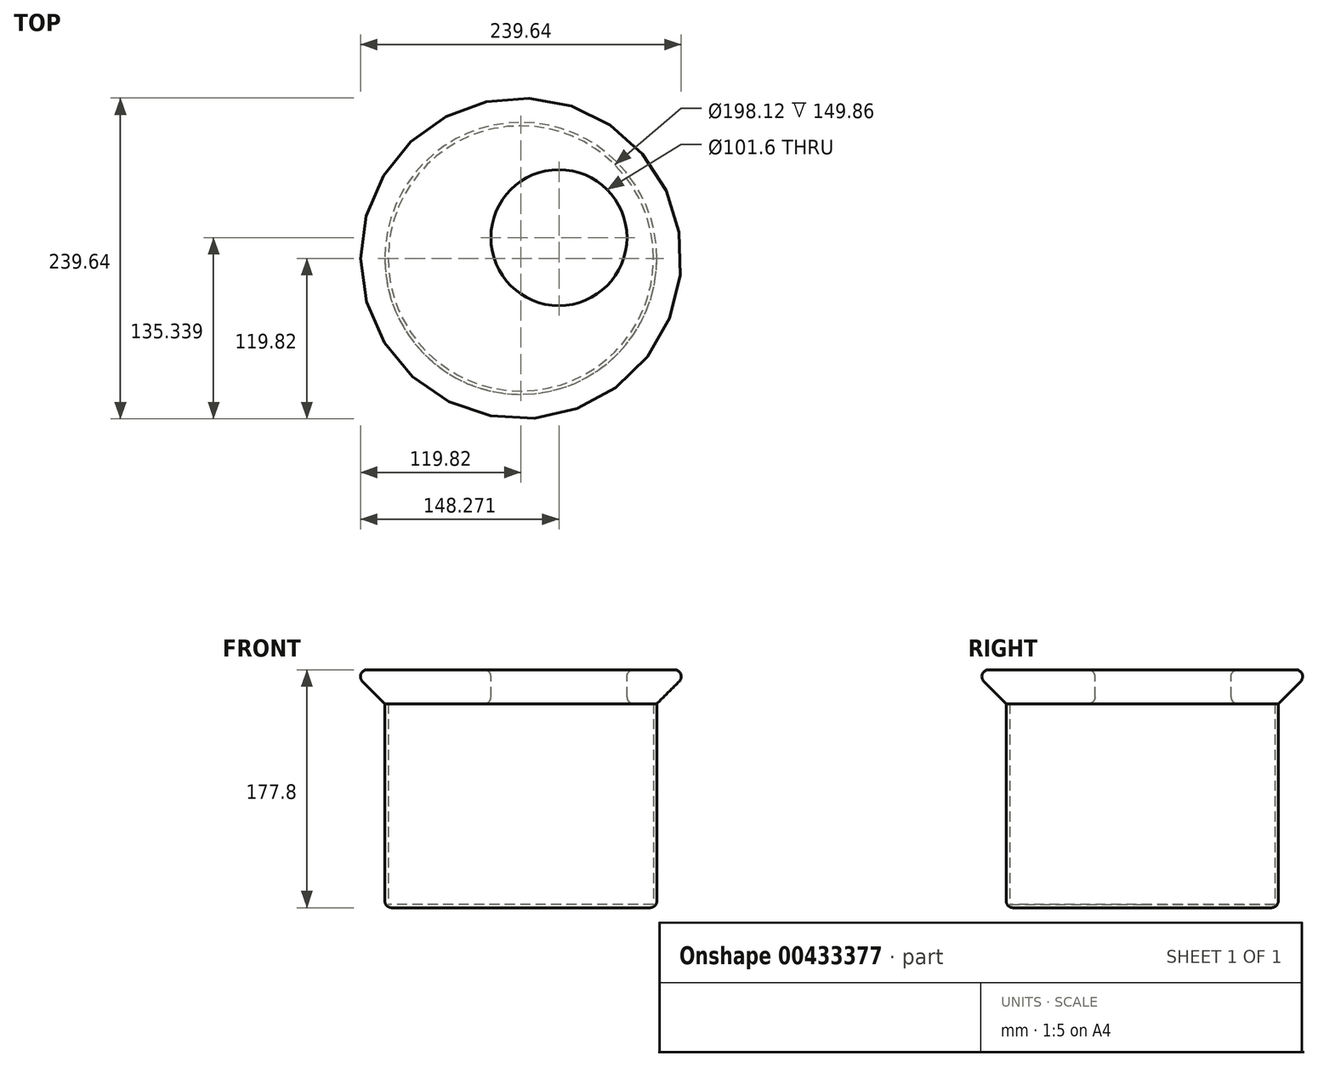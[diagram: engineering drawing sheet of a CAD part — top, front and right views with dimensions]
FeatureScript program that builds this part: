
annotation { "Feature Type Name" : "Feature", "Feature Type Description" : "" }
export const myFeature = defineFeature(function(context is Context, id is Id, definition is map)
    precondition{}
    {
        {
            var Q0;
            Q0=qCreatedBy(makeId("Front.planeOp"),FACE);
            var sketch = newSketch(context, id + "F0", { "sketchPlane" : qUnion([Q0])});
            skLineSegment(sketch, "E0", {"start": v(-127, 57.85) * mm, "end": v(0, 57.85) * mm});
            skLineSegment(sketch, "E1", {"start": v(-127, 57.85) * mm, "end": v(-101.6, 32.45) * mm});
            skLineSegment(sketch, "E2", {"start": v(-101.6, 32.45) * mm, "end": v(0, 32.45) * mm});
            skLineSegment(sketch, "E3", {"start": v(0, 57.85) * mm, "end": v(0, 32.45) * mm});
            skSolve(sketch);
        }
        {
            var Q0;
            Q0=makeQuery(id+"F0.imprint","IMPRINT",FACE,{"disambiguationData":[TD([[makeQuery(id+"F0.imprint","IMPRINT",EDGE,{"derivedFrom":sQuery(id+"F0.wireOp",EDGE,"E0")}),-1.0]])]});
            var Q1;
            Q1=sQuery(id+"F0.wireOp",EDGE,"E3");
            revolve(context, id + "F1", {"entities" : qUnion([Q0]), "axis" : qUnion([Q1]), "revolveType" : RevolveType.FULL});
        }
        {
            var Q0;
            Q0=makeQuery(id+"F1.opRevolve","SWEPT_FACE",FACE,{"disambiguationData":[OSD([sQuery(id+"F0.wireOp",EDGE,"E0")])]});
            var sketch = newSketch(context, id + "F2", { "sketchPlane" : qUnion([Q0])});
            skCircle(sketch, "E4", {"center": v(28.45, 15.52) * mm, "radius": 50.8 * mm});
            skSolve(sketch);
        }
        {
            var Q0;
            Q0 = qSketchRegion(id + "F2", true);
            extrude(context, id + "F3", {"entities" : qUnion([Q0]), "operationType" : NewBodyOperationType.REMOVE, "oppositeDirection" : true, "depth" : 31.5 * mm});
        }
        {
            var Q0;
            Q0=qCreatedBy(makeId("Front.planeOp"),FACE);
            var sketch = newSketch(context, id + "F4", { "sketchPlane" : qUnion([Q0])});
            skLineSegment(sketch, "E5", {"start": v(-101.6, 32.45) * mm, "end": v(-101.6, -119.95) * mm});
            skLineSegment(sketch, "E6", {"start": v(-101.6, -119.95) * mm, "end": v(0, -119.95) * mm});
            skLineSegment(sketch, "E7", {"start": v(-101.6, 32.45) * mm, "end": v(0, 32.45) * mm});
            skLineSegment(sketch, "E8", {"start": v(0, -119.95) * mm, "end": v(0, 32.45) * mm});
            skSolve(sketch);
        }
        {
            var Q0;
            Q0=makeQuery(id+"F4.imprint","IMPRINT",FACE,{"disambiguationData":[TD([[makeQuery(id+"F4.imprint","IMPRINT",EDGE,{"derivedFrom":sQuery(id+"F4.wireOp",EDGE,"E5")}),1.0]])]});
            var Q1;
            Q1=sQuery(id+"F4.wireOp",EDGE,"E8");
            revolve(context, id + "F5", {"entities" : qUnion([Q0]), "axis" : qUnion([Q1]), "revolveType" : RevolveType.FULL});
        }
        {
            var Q0;
            Q0=makeQuery(id+"F5.opRevolve","SWEPT_FACE",FACE,{"disambiguationData":[OSD([sQuery(id+"F4.wireOp",EDGE,"E7")])]});
            shell(context, id + "F6", {"entities" : qUnion([Q0]), "thickness" : 2.54 * mm});
        }
        {
            var Q0;
            Q0=makeQuery(id+"F1.opRevolve","SWEPT_FACE",FACE,{"disambiguationData":[OSD([sQuery(id+"F0.wireOp",EDGE,"E0")])]});
            var Q1;
            Q1=makeQuery(id+"F5.opRevolve","SWEPT_FACE",FACE,{"disambiguationData":[OSD([sQuery(id+"F4.wireOp",EDGE,"E6")])]});
            fillet(context, id + "F7", {"entities" : qUnion([Q0, Q1]), "radius" : 5.08 * mm, "tangentPropagation" : true, "allowEdgeOverflow" : false});
        }
        {
            var Q0;
            Q0=makeQuery(id+"F3.boolean.opBoolean","COPY",FACE,{"derivedFrom":makeQuery(id+"F3.opExtrude","SWEPT_FACE",FACE,{"disambiguationData":[OSD([sQuery(id+"F2.wireOp",EDGE,"E4")])]})});
            fillet(context, id + "F8", {"entities" : qUnion([Q0]), "radius" : 5.08 * mm, "tangentPropagation" : true, "allowEdgeOverflow" : false});
        }
    });
